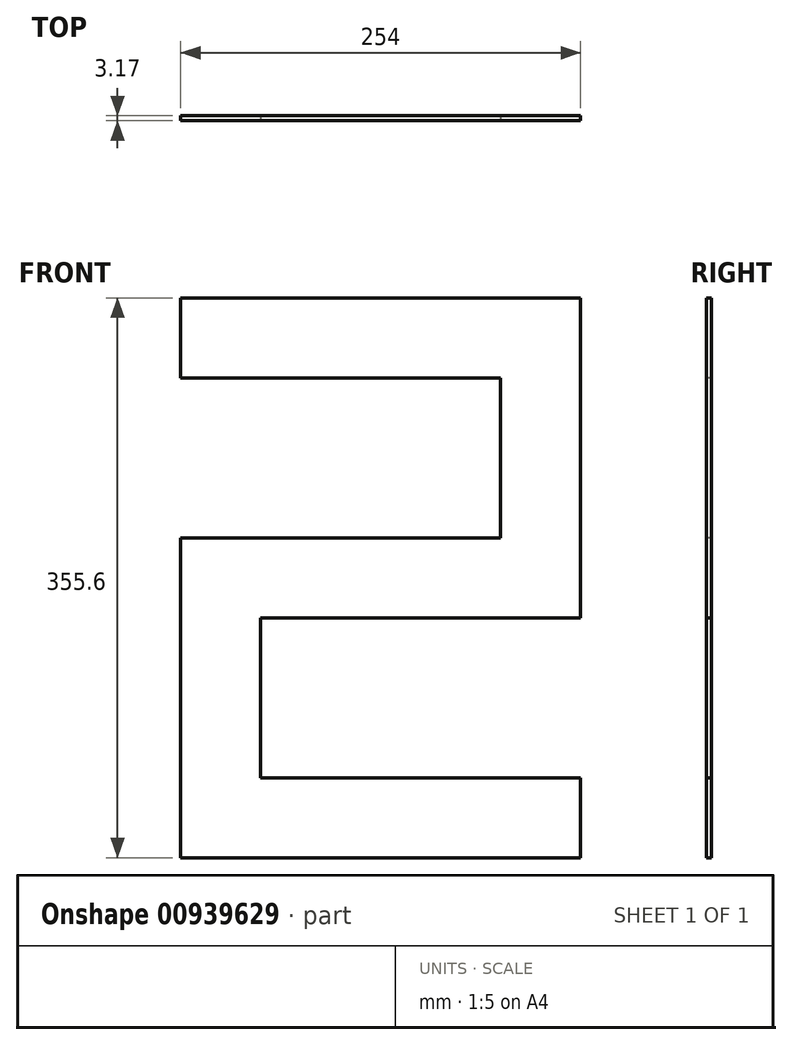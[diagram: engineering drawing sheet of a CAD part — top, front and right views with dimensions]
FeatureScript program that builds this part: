
annotation { "Feature Type Name" : "Feature", "Feature Type Description" : "" }
export const myFeature = defineFeature(function(context is Context, id is Id, definition is map)
    precondition{}
    {
        {
            var Q0;
            Q0=qCreatedBy(makeId("Front.planeOp"),FACE);
            var sketch = newSketch(context, id + "F0", { "sketchPlane" : qUnion([Q0])});
            skLineSegment(sketch, "E0.bottom", {"start": v(0, 0) * mm, "end": v(-254, 0) * mm});
            skLineSegment(sketch, "E0.top", {"start": v(0, 50.8) * mm, "end": v(-254, 50.8) * mm});
            skLineSegment(sketch, "E0.left", {"start": v(0, 0) * mm, "end": v(0, 50.8) * mm});
            skLineSegment(sketch, "E0.right", {"start": v(-254, 0) * mm, "end": v(-254, 50.8) * mm});
            skLineSegment(sketch, "E1.bottom", {"start": v(-254, 50.8) * mm, "end": v(-203.2, 50.8) * mm});
            skLineSegment(sketch, "E1.top", {"start": v(-254, 152.4) * mm, "end": v(-203.2, 152.4) * mm});
            skLineSegment(sketch, "E1.left", {"start": v(-254, 50.8) * mm, "end": v(-254, 152.4) * mm});
            skLineSegment(sketch, "E1.right", {"start": v(-203.2, 50.8) * mm, "end": v(-203.2, 152.4) * mm});
            skLineSegment(sketch, "E2.bottom", {"start": v(-254, 152.4) * mm, "end": v(0, 152.4) * mm});
            skLineSegment(sketch, "E2.top", {"start": v(-254, 203.2) * mm, "end": v(0, 203.2) * mm});
            skLineSegment(sketch, "E2.left", {"start": v(-254, 152.4) * mm, "end": v(-254, 203.2) * mm});
            skLineSegment(sketch, "E2.right", {"start": v(0, 152.4) * mm, "end": v(0, 203.2) * mm});
            skLineSegment(sketch, "E3.bottom", {"start": v(0, 203.2) * mm, "end": v(-50.8, 203.2) * mm});
            skLineSegment(sketch, "E3.top", {"start": v(0, 304.8) * mm, "end": v(-50.8, 304.8) * mm});
            skLineSegment(sketch, "E3.left", {"start": v(0, 203.2) * mm, "end": v(0, 304.8) * mm});
            skLineSegment(sketch, "E3.right", {"start": v(-50.8, 203.2) * mm, "end": v(-50.8, 304.8) * mm});
            skLineSegment(sketch, "E4.bottom", {"start": v(0, 304.8) * mm, "end": v(-254, 304.8) * mm});
            skLineSegment(sketch, "E4.top", {"start": v(0, 355.6) * mm, "end": v(-254, 355.6) * mm});
            skLineSegment(sketch, "E4.left", {"start": v(0, 304.8) * mm, "end": v(0, 355.6) * mm});
            skLineSegment(sketch, "E4.right", {"start": v(-254, 304.8) * mm, "end": v(-254, 355.6) * mm});
            skSolve(sketch);
        }
        {
            var Q0;
            Q0 = qSketchRegion(id + "F0", true);
            extrude(context, id + "F1", {"entities" : qUnion([Q0]), "oppositeDirection" : true, "depth" : 3.17 * mm, "offsetDistance" : 25.4 * mm});
        }
    });
